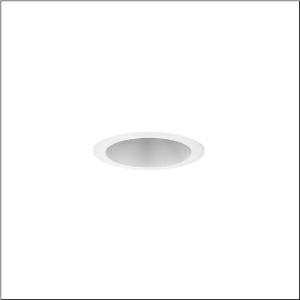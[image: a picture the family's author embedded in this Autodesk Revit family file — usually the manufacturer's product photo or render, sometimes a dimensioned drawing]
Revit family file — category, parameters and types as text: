
# Revit family: lunis_31_mini_51dn157e41
name_source: partatom
category: Lighting Fixtures
units: mm (PartAtom-declared; Revit-internal decimal feet)

## family parameters
Cut with Voids When Loaded = No
Host = Face
Light Source = No
Part Type = Normal
Room Calculation Point = No
Round Connector Dimension = Use Diameter
Shared = No

## types (1)
- Lunis 31 mini (1 x LED, 1040 lm, 8.3 W, 4000K)
    Apparent Load = 8 VA
    CIE Flux Codes = 93 98 100 100 100
    Color Rendering = 80
    Color Temperature = 4000K
    Default Elevation = 1800 mm
    Description = Lunis 31,  mini, downlight, light control with lens, light emission: direct distribution, LED rated luminous flux: 1.040lm, light colour: 840, mains connection: 220..240V, AC, 50/60Hz, housing, white, protection rating (complete): IP20, protection rating (on room side): IP54, insulation class (complete): insulation class II (safety insulation), certification: CE, packaging unit: 1 piece
    Height = 0 mm  [stored 0 ft]
    Lamp = 1 x LED
    Lamp Light Flux = 1040 lm
    Lamp Power = 8.3 W
    Lamp count = 1
    Length = 188 mm  [stored 0.616798 ft]
    Luminous efficacy = 125 lm/W
    Manufacturer = Siteco
    ModVariant = No
    Model = 51DN157E41
    Mounting Place = Ceiling
    Mounting Type = Recessed
    Number of Poles = 1
    OnlyDefault = Yes
    Power Factor = 1
    Product Name = Lunis 31 mini
    Product group = downlight
    ProductGroupID = 400
    Protection Class = Protection class II
    Protection Degree = IP 20
    RLX_Detail_Level = 1
    RLX_Emergency_Light_Flux = 0 lm
    RLX_Emergency_Type = 0
    RLX_Emergency_Type_DB = No
    RlxData = <blob elided: 21817 chars, md5=43eec584>
    Socket = socket
    Standby Power = 0 W
    System Light Flux = 1040 lm
    System Power = 8 W
    Type Comments = Product without accessories
    Type Image = l_1005624.jpg
    URL = http://relux.com
    VarID = ---
    Voltage = 0 V
    Weight = 0.00 kg
    Width = 0 mm  [stored 0 ft]

note: [stored X ft] marks values corroborated as IEEE doubles in the binary element streams (Revit-internal decimal feet)

## geometry (parser evidence)
native form markers: Blend x4, Sweep x13
no freeform markers — native parametric forms only
